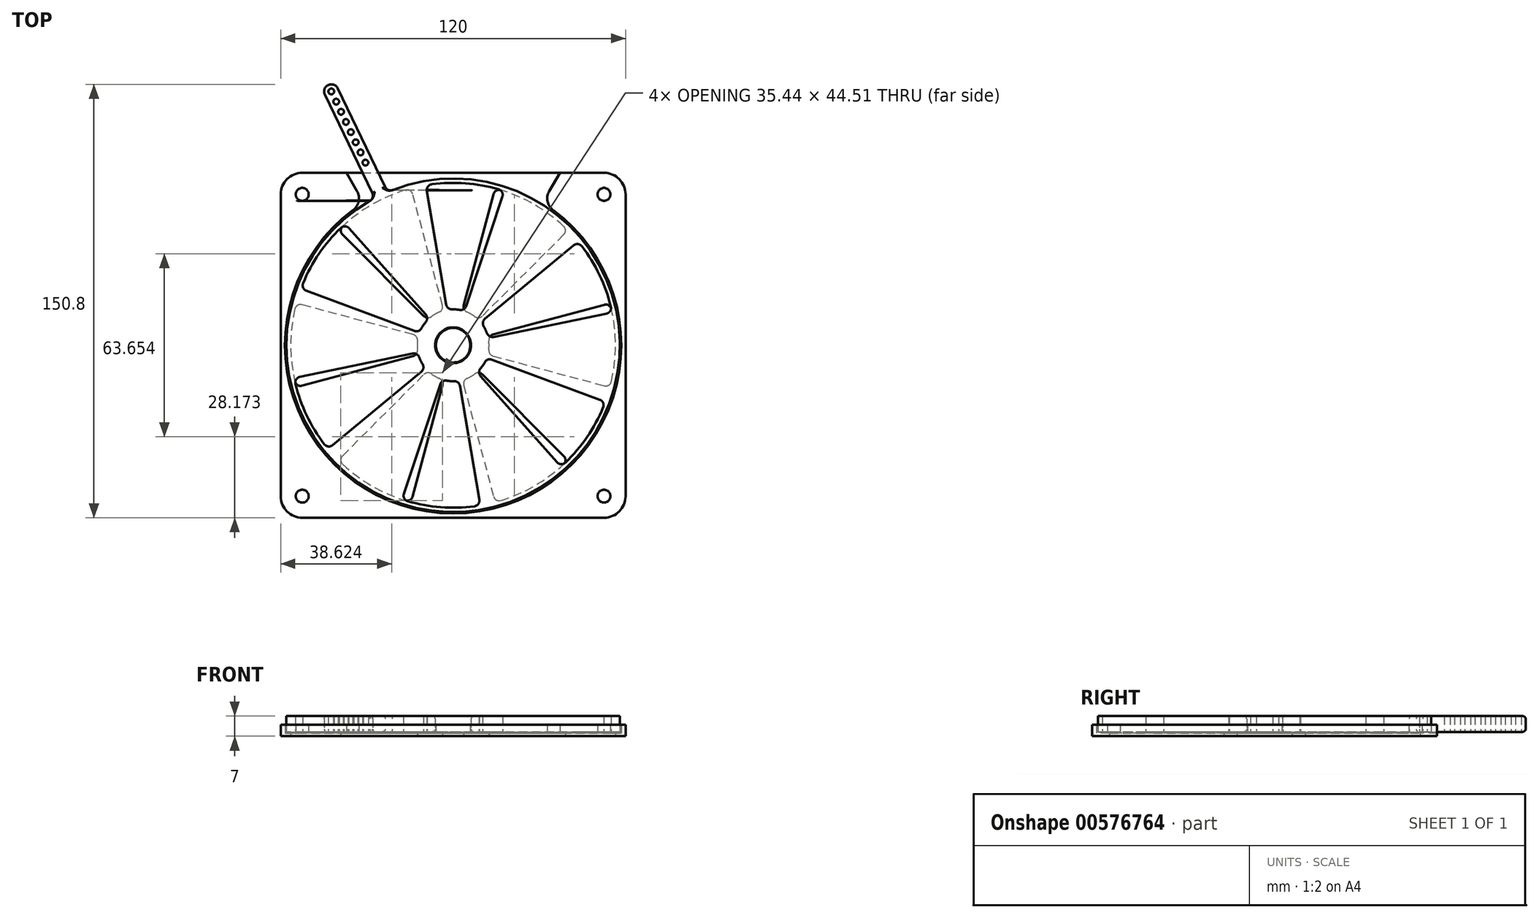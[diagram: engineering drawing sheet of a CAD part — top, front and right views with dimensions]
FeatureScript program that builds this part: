
annotation { "Feature Type Name" : "Feature", "Feature Type Description" : "" }
export const myFeature = defineFeature(function(context is Context, id is Id, definition is map)
    precondition{}
    {
        {
            var Q0;
            Q0=qCreatedBy(makeId("Top.planeOp"),FACE);
            var sketch = newSketch(context, id + "F0", { "sketchPlane" : qUnion([Q0])});
            skLineSegment(sketch, "E0.0", {"start": v(-52.5, 60) * mm, "end": v(52.5, 60) * mm});
            skLineSegment(sketch, "E0.1", {"start": v(-60, -52.5) * mm, "end": v(-60, 52.5) * mm});
            skLineSegment(sketch, "E0.2", {"start": v(-52.5, -60) * mm, "end": v(52.5, -60) * mm});
            skLineSegment(sketch, "E0.3", {"start": v(60, -52.5) * mm, "end": v(60, 52.5) * mm});
            skArc(sketch, "E1", {"start": v(52.5, 60) * mm, "mid": v(57.8, 57.8) * mm, "end": v(60, 52.5) * mm});
            skArc(sketch, "E2.1.1", {"start": v(-60, 52.5) * mm, "mid": v(-57.8, 57.8) * mm, "end": v(-52.5, 60) * mm});
            skArc(sketch, "E2.2.1", {"start": v(-52.5, -60) * mm, "mid": v(-57.8, -57.8) * mm, "end": v(-60, -52.5) * mm});
            skArc(sketch, "E2.3.1", {"start": v(60, -52.5) * mm, "mid": v(57.8, -57.8) * mm, "end": v(52.5, -60) * mm});
            skPoint(sketch, "E2.center", {"position": v(0, 0) * mm});
            skCircle(sketch, "E3", {"center": v(0, 0) * mm, "radius": 58.5 * mm});
            skCircle(sketch, "E4", {"center": v(-52.5, 52.5) * mm, "radius": 2.25 * mm});
            skCircle(sketch, "E5", {"center": v(52.5, 52.5) * mm, "radius": 2.25 * mm});
            skCircle(sketch, "E6", {"center": v(52.5, -52.5) * mm, "radius": 2.25 * mm});
            skCircle(sketch, "E7", {"center": v(-52.5, -52.5) * mm, "radius": 2.25 * mm});
            skCircle(sketch, "E8.0", {"center": v(0, 0) * mm, "radius": 56.5 * mm});
            skCircle(sketch, "E9", {"center": v(0, 0) * mm, "radius": 12.5 * mm});
            skLineSegment(sketch, "E10", {"start": v(-29.25, 50.66) * mm, "end": v(-34.64, 60) * mm});
            skLineSegment(sketch, "E11", {"start": v(29.25, 50.66) * mm, "end": v(34.64, 60) * mm});
            skLineSegment(sketch, "E12", {"start": v(-31.1, 49.55) * mm, "end": v(-37.14, 60) * mm});
            skLineSegment(sketch, "E13", {"start": v(37.14, 60) * mm, "end": v(31.1, 49.55) * mm});
            skCircle(sketch, "E14", {"center": v(0, 0) * mm, "radius": 6 * mm});
            skLineSegment(sketch, "E15.2.5.0", {"start": v(14.62, 54.57) * mm, "end": v(0, 0) * mm});
            skLineSegment(sketch, "E16.2.3.0", {"start": v(0, 0) * mm, "end": v(-14.62, 54.57) * mm});
            skLineSegment(sketch, "E17", {"start": v(-29.25, 50.66) * mm, "end": v(0, 0) * mm, "construction": true});
            skLineSegment(sketch, "E18.1.0", {"start": v(0, 0) * mm, "end": v(-54.57, 14.62) * mm});
            skLineSegment(sketch, "E18.1.1", {"start": v(-39.95, 39.95) * mm, "end": v(0, 0) * mm});
            skLineSegment(sketch, "E18.2.0", {"start": v(-39.95, -39.95) * mm, "end": v(0, 0) * mm});
            skLineSegment(sketch, "E18.2.1", {"start": v(-54.57, -14.62) * mm, "end": v(0, 0) * mm});
            skLineSegment(sketch, "E18.3.0", {"start": v(0, 0) * mm, "end": v(14.62, -54.57) * mm});
            skLineSegment(sketch, "E18.3.1", {"start": v(-14.62, -54.57) * mm, "end": v(0, 0) * mm});
            skLineSegment(sketch, "E18.4.0", {"start": v(0, 0) * mm, "end": v(54.57, -14.62) * mm});
            skLineSegment(sketch, "E18.4.1", {"start": v(39.95, -39.95) * mm, "end": v(0, 0) * mm});
            skLineSegment(sketch, "E18.5.0", {"start": v(39.95, 39.95) * mm, "end": v(0, 0) * mm});
            skLineSegment(sketch, "E18.5.1", {"start": v(54.57, 14.62) * mm, "end": v(0, 0) * mm});
            skLineSegment(sketch, "E19", {"start": v(29.25, 50.66) * mm, "end": v(0, 0) * mm, "construction": true});
            skSolve(sketch);
        }
        {
            var Q0;
            Q0=makeQuery(id+"F0.imprint","IMPRINT",FACE,{"disambiguationData":[TD([[makeQuery(id+"F0.imprint","IMPRINT",EDGE,{"derivedFrom":sQuery(id+"F0.wireOp",EDGE,"E0.1")}),-1.0]])]});
            extrude(context, id + "F1", {"entities" : qUnion([Q0]), "depth" : 4 * mm, "offsetDistance" : 25 * mm});
        }
        {
            var Q0;
            {var subQ0=sQuery(id+"F0.wireOp",EDGE,"E18.5.0");var subQ1=sQuery(id+"F0.wireOp",EDGE,"E9");var subQ2=makeQuery(id+"F0.imprint","INTERSECT",VERTEX,{"derivedFrom":[subQ1,subQ0]});Q0=makeQuery(id+"F0.imprint","IMPRINT",FACE,{"disambiguationData":[TD([[makeQuery(id+"F0.imprint","IMPRINT",EDGE,{"disambiguationData":[TD([[subQ2,1.0]])],"derivedFrom":subQ1}),1.0]])]});}
            var Q1;
            {var subQ0=sQuery(id+"F0.wireOp",EDGE,"E15.2.5.0");var subQ1=sQuery(id+"F0.wireOp",EDGE,"E9");var subQ2=makeQuery(id+"F0.imprint","INTERSECT",VERTEX,{"derivedFrom":[subQ1,subQ0]});Q1=makeQuery(id+"F0.imprint","IMPRINT",FACE,{"disambiguationData":[TD([[makeQuery(id+"F0.imprint","IMPRINT",EDGE,{"disambiguationData":[TD([[subQ2,-1.0]])],"derivedFrom":subQ1}),1.0]])]});}
            var Q2;
            {var subQ0=sQuery(id+"F0.wireOp",EDGE,"E16.2.3.0");var subQ1=sQuery(id+"F0.wireOp",EDGE,"E9");var subQ2=makeQuery(id+"F0.imprint","INTERSECT",VERTEX,{"derivedFrom":[subQ1,subQ0]});Q2=makeQuery(id+"F0.imprint","IMPRINT",FACE,{"disambiguationData":[TD([[makeQuery(id+"F0.imprint","IMPRINT",EDGE,{"disambiguationData":[TD([[subQ2,-1.0]])],"derivedFrom":subQ1}),1.0]])]});}
            var Q3;
            {var subQ0=sQuery(id+"F0.wireOp",EDGE,"E18.1.1");var subQ1=sQuery(id+"F0.wireOp",EDGE,"E9");var subQ2=makeQuery(id+"F0.imprint","INTERSECT",VERTEX,{"derivedFrom":[subQ1,subQ0]});Q3=makeQuery(id+"F0.imprint","IMPRINT",FACE,{"disambiguationData":[TD([[makeQuery(id+"F0.imprint","IMPRINT",EDGE,{"disambiguationData":[TD([[subQ2,-1.0]])],"derivedFrom":subQ1}),1.0]])]});}
            var Q4;
            {var subQ0=sQuery(id+"F0.wireOp",EDGE,"E18.1.0");var subQ1=sQuery(id+"F0.wireOp",EDGE,"E9");var subQ2=makeQuery(id+"F0.imprint","INTERSECT",VERTEX,{"derivedFrom":[subQ1,subQ0]});Q4=makeQuery(id+"F0.imprint","IMPRINT",FACE,{"disambiguationData":[TD([[makeQuery(id+"F0.imprint","IMPRINT",EDGE,{"disambiguationData":[TD([[subQ2,-1.0]])],"derivedFrom":subQ1}),1.0]])]});}
            var Q5;
            {var subQ0=sQuery(id+"F0.wireOp",EDGE,"E18.2.1");var subQ1=sQuery(id+"F0.wireOp",EDGE,"E9");var subQ2=makeQuery(id+"F0.imprint","INTERSECT",VERTEX,{"derivedFrom":[subQ1,subQ0]});Q5=makeQuery(id+"F0.imprint","IMPRINT",FACE,{"disambiguationData":[TD([[makeQuery(id+"F0.imprint","IMPRINT",EDGE,{"disambiguationData":[TD([[subQ2,-1.0]])],"derivedFrom":subQ1}),1.0]])]});}
            var Q6;
            {var subQ0=sQuery(id+"F0.wireOp",EDGE,"E18.2.0");var subQ1=sQuery(id+"F0.wireOp",EDGE,"E9");var subQ2=makeQuery(id+"F0.imprint","INTERSECT",VERTEX,{"derivedFrom":[subQ1,subQ0]});Q6=makeQuery(id+"F0.imprint","IMPRINT",FACE,{"disambiguationData":[TD([[makeQuery(id+"F0.imprint","IMPRINT",EDGE,{"disambiguationData":[TD([[subQ2,-1.0]])],"derivedFrom":subQ1}),1.0]])]});}
            var Q7;
            {var subQ0=sQuery(id+"F0.wireOp",EDGE,"E18.3.1");var subQ1=sQuery(id+"F0.wireOp",EDGE,"E9");var subQ2=makeQuery(id+"F0.imprint","INTERSECT",VERTEX,{"derivedFrom":[subQ1,subQ0]});Q7=makeQuery(id+"F0.imprint","IMPRINT",FACE,{"disambiguationData":[TD([[makeQuery(id+"F0.imprint","IMPRINT",EDGE,{"disambiguationData":[TD([[subQ2,-1.0]])],"derivedFrom":subQ1}),1.0]])]});}
            var Q8;
            {var subQ0=sQuery(id+"F0.wireOp",EDGE,"E18.3.0");var subQ1=sQuery(id+"F0.wireOp",EDGE,"E9");var subQ2=makeQuery(id+"F0.imprint","INTERSECT",VERTEX,{"derivedFrom":[subQ1,subQ0]});Q8=makeQuery(id+"F0.imprint","IMPRINT",FACE,{"disambiguationData":[TD([[makeQuery(id+"F0.imprint","IMPRINT",EDGE,{"disambiguationData":[TD([[subQ2,-1.0]])],"derivedFrom":subQ1}),1.0]])]});}
            var Q9;
            {var subQ0=sQuery(id+"F0.wireOp",EDGE,"E18.4.1");var subQ1=sQuery(id+"F0.wireOp",EDGE,"E9");var subQ2=makeQuery(id+"F0.imprint","INTERSECT",VERTEX,{"derivedFrom":[subQ1,subQ0]});Q9=makeQuery(id+"F0.imprint","IMPRINT",FACE,{"disambiguationData":[TD([[makeQuery(id+"F0.imprint","IMPRINT",EDGE,{"disambiguationData":[TD([[subQ2,-1.0]])],"derivedFrom":subQ1}),1.0]])]});}
            var Q10;
            {var subQ0=sQuery(id+"F0.wireOp",EDGE,"E18.5.1");var subQ1=sQuery(id+"F0.wireOp",EDGE,"E9");var subQ2=makeQuery(id+"F0.imprint","INTERSECT",VERTEX,{"derivedFrom":[subQ1,subQ0]});Q10=makeQuery(id+"F0.imprint","IMPRINT",FACE,{"disambiguationData":[TD([[makeQuery(id+"F0.imprint","IMPRINT",EDGE,{"disambiguationData":[TD([[subQ2,1.0]])],"derivedFrom":subQ1}),1.0]])]});}
            var Q11;
            {var subQ0=sQuery(id+"F0.wireOp",EDGE,"E11");Q11=makeQuery(id+"F0.imprint","IMPRINT",FACE,{"disambiguationData":[TD([[makeQuery(id+"F0.imprint","IMPRINT",EDGE,{"derivedFrom":subQ0}),-1.0]])]});}
            var Q12;
            {var subQ0=sQuery(id+"F0.wireOp",EDGE,"E18.5.0");var subQ1=sQuery(id+"F0.wireOp",EDGE,"E9");var subQ2=makeQuery(id+"F0.imprint","INTERSECT",VERTEX,{"derivedFrom":[subQ1,subQ0]});Q12=makeQuery(id+"F0.imprint","IMPRINT",FACE,{"disambiguationData":[TD([[makeQuery(id+"F0.imprint","IMPRINT",EDGE,{"disambiguationData":[TD([[subQ2,-1.0]])],"derivedFrom":subQ1}),1.0]])]});}
            var Q13;
            {var subQ0=sQuery(id+"F0.wireOp",EDGE,"E10");Q13=makeQuery(id+"F0.imprint","IMPRINT",FACE,{"disambiguationData":[TD([[makeQuery(id+"F0.imprint","IMPRINT",EDGE,{"derivedFrom":subQ0}),-1.0]])]});}
            var Q14;
            {var subQ6=sQuery(id+"F0.wireOp",EDGE,"E3");var subQ7=makeQuery(id+"F0.imprint","INTERSECT",VERTEX,{"derivedFrom":[subQ6,sQuery(id+"F0.wireOp",EDGE,"E11")]});Q14=makeQuery(id+"F0.imprint","IMPRINT",FACE,{"disambiguationData":[TD([[makeQuery(id+"F0.imprint","IMPRINT",EDGE,{"disambiguationData":[TD([[subQ7,1.0]])],"derivedFrom":subQ6}),1.0]])]});}
            var Q15;
            {var subQ0=sQuery(id+"F0.wireOp",EDGE,"E10");Q15=makeQuery(id+"F0.imprint","IMPRINT",FACE,{"disambiguationData":[TD([[makeQuery(id+"F0.imprint","IMPRINT",EDGE,{"derivedFrom":subQ0}),1.0]])]});}
            var Q16;
            {var subQ0=sQuery(id+"F0.wireOp",EDGE,"E18.5.0");var subQ1=sQuery(id+"F0.wireOp",EDGE,"E8.0");var subQ2=makeQuery(id+"F0.imprint","INTERSECT",VERTEX,{"derivedFrom":[subQ1,subQ0]});Q16=makeQuery(id+"F0.imprint","IMPRINT",FACE,{"disambiguationData":[TD([[makeQuery(id+"F0.imprint","IMPRINT",EDGE,{"disambiguationData":[TD([[subQ2,1.0]])],"derivedFrom":subQ1}),1.0]])]});}
            var Q17;
            {var subQ0=sQuery(id+"F0.wireOp",EDGE,"E18.4.0");var subQ1=sQuery(id+"F0.wireOp",EDGE,"E8.0");var subQ2=makeQuery(id+"F0.imprint","INTERSECT",VERTEX,{"derivedFrom":[subQ1,subQ0]});Q17=makeQuery(id+"F0.imprint","IMPRINT",FACE,{"disambiguationData":[TD([[makeQuery(id+"F0.imprint","IMPRINT",EDGE,{"disambiguationData":[TD([[subQ2,1.0]])],"derivedFrom":subQ1}),1.0]])]});}
            var Q18;
            {var subQ0=sQuery(id+"F0.wireOp",EDGE,"E18.3.0");var subQ1=sQuery(id+"F0.wireOp",EDGE,"E8.0");var subQ2=makeQuery(id+"F0.imprint","INTERSECT",VERTEX,{"derivedFrom":[subQ1,subQ0]});Q18=makeQuery(id+"F0.imprint","IMPRINT",FACE,{"disambiguationData":[TD([[makeQuery(id+"F0.imprint","IMPRINT",EDGE,{"disambiguationData":[TD([[subQ2,1.0]])],"derivedFrom":subQ1}),1.0]])]});}
            var Q19;
            {var subQ0=sQuery(id+"F0.wireOp",EDGE,"E18.2.0");var subQ1=sQuery(id+"F0.wireOp",EDGE,"E8.0");var subQ2=makeQuery(id+"F0.imprint","INTERSECT",VERTEX,{"derivedFrom":[subQ1,subQ0]});Q19=makeQuery(id+"F0.imprint","IMPRINT",FACE,{"disambiguationData":[TD([[makeQuery(id+"F0.imprint","IMPRINT",EDGE,{"disambiguationData":[TD([[subQ2,1.0]])],"derivedFrom":subQ1}),1.0]])]});}
            var Q20;
            {var subQ0=sQuery(id+"F0.wireOp",EDGE,"E18.1.0");var subQ1=sQuery(id+"F0.wireOp",EDGE,"E8.0");var subQ2=makeQuery(id+"F0.imprint","INTERSECT",VERTEX,{"derivedFrom":[subQ1,subQ0]});Q20=makeQuery(id+"F0.imprint","IMPRINT",FACE,{"disambiguationData":[TD([[makeQuery(id+"F0.imprint","IMPRINT",EDGE,{"disambiguationData":[TD([[subQ2,1.0]])],"derivedFrom":subQ1}),1.0]])]});}
            var Q21;
            {var subQ0=sQuery(id+"F0.wireOp",EDGE,"E15.2.5.0");var subQ1=sQuery(id+"F0.wireOp",EDGE,"E8.0");var subQ2=makeQuery(id+"F0.imprint","INTERSECT",VERTEX,{"derivedFrom":[subQ1,subQ0]});Q21=makeQuery(id+"F0.imprint","IMPRINT",FACE,{"disambiguationData":[TD([[makeQuery(id+"F0.imprint","IMPRINT",EDGE,{"disambiguationData":[TD([[subQ2,-1.0]])],"derivedFrom":subQ1}),1.0]])]});}
            extrude(context, id + "F2", {"entities" : qUnion([Q0, Q1, Q2, Q3, Q4, Q5, Q6, Q7, Q8, Q9, Q10, Q11, Q12, Q13, Q14, Q15, Q16, Q17, Q18, Q19, Q20, Q21]), "operationType" : NewBodyOperationType.ADD, "depth" : 1 * mm, "offsetDistance" : 25 * mm});
        }
        {
            var Q0;
            {var subQ0=sQuery(id+"F0.wireOp",EDGE,"E15.2.5.0");var subQ1=sQuery(id+"F0.wireOp",EDGE,"E14");var subQ2=makeQuery(id+"F0.imprint","INTERSECT",VERTEX,{"disambiguationData":[OD(1.0)],"derivedFrom":[subQ1,subQ0]});Q0=makeQuery(id+"F0.imprint","IMPRINT",FACE,{"disambiguationData":[TD([[makeQuery(id+"F0.imprint","IMPRINT",EDGE,{"disambiguationData":[TD([[subQ2,-1.0]])],"derivedFrom":subQ1}),1.0]])]});}
            var Q1;
            {var subQ0=sQuery(id+"F0.wireOp",EDGE,"E16.2.4.0");var subQ1=sQuery(id+"F0.wireOp",EDGE,"E14");var subQ2=makeQuery(id+"F0.imprint","INTERSECT",VERTEX,{"disambiguationData":[OD(1.0)],"derivedFrom":[subQ1,subQ0]});Q1=makeQuery(id+"F0.imprint","IMPRINT",FACE,{"disambiguationData":[TD([[makeQuery(id+"F0.imprint","IMPRINT",EDGE,{"disambiguationData":[TD([[subQ2,-1.0]])],"derivedFrom":subQ1}),1.0]])]});}
            var Q2;
            {var subQ0=sQuery(id+"F0.wireOp",EDGE,"E16.2.3.0");var subQ1=sQuery(id+"F0.wireOp",EDGE,"E14");var subQ2=makeQuery(id+"F0.imprint","INTERSECT",VERTEX,{"disambiguationData":[OD(1.0)],"derivedFrom":[subQ1,subQ0]});Q2=makeQuery(id+"F0.imprint","IMPRINT",FACE,{"disambiguationData":[TD([[makeQuery(id+"F0.imprint","IMPRINT",EDGE,{"disambiguationData":[TD([[subQ2,-1.0]])],"derivedFrom":subQ1}),1.0]])]});}
            var Q3;
            {var subQ0=sQuery(id+"F0.wireOp",EDGE,"874d3e22-e00a-4f2a-9944-a1ca78a42176.2.0");var subQ1=sQuery(id+"F0.wireOp",EDGE,"E14");var subQ2=makeQuery(id+"F0.imprint","INTERSECT",VERTEX,{"disambiguationData":[OD(1.0)],"derivedFrom":[subQ1,subQ0]});Q3=makeQuery(id+"F0.imprint","IMPRINT",FACE,{"disambiguationData":[TD([[makeQuery(id+"F0.imprint","IMPRINT",EDGE,{"disambiguationData":[TD([[subQ2,-1.0]])],"derivedFrom":subQ1}),1.0]])]});}
            var Q4;
            {var subQ0=sQuery(id+"F0.wireOp",EDGE,"E15.2.5.0");var subQ1=sQuery(id+"F0.wireOp",EDGE,"E14");var subQ2=makeQuery(id+"F0.imprint","INTERSECT",VERTEX,{"disambiguationData":[OD(0.0)],"derivedFrom":[subQ1,subQ0]});Q4=makeQuery(id+"F0.imprint","IMPRINT",FACE,{"disambiguationData":[TD([[makeQuery(id+"F0.imprint","IMPRINT",EDGE,{"disambiguationData":[TD([[subQ2,1.0]])],"derivedFrom":subQ1}),1.0]])]});}
            var Q5;
            {var subQ0=sQuery(id+"F0.wireOp",EDGE,"E16.2.5.0");var subQ1=sQuery(id+"F0.wireOp",EDGE,"E14");var subQ2=makeQuery(id+"F0.imprint","INTERSECT",VERTEX,{"disambiguationData":[OD(0.0)],"derivedFrom":[subQ1,subQ0]});Q5=makeQuery(id+"F0.imprint","IMPRINT",FACE,{"disambiguationData":[TD([[makeQuery(id+"F0.imprint","IMPRINT",EDGE,{"disambiguationData":[TD([[subQ2,1.0]])],"derivedFrom":subQ1}),1.0]])]});}
            var Q6;
            {var subQ0=sQuery(id+"F0.wireOp",EDGE,"E16.2.5.0");var subQ1=sQuery(id+"F0.wireOp",EDGE,"E14");var subQ2=makeQuery(id+"F0.imprint","INTERSECT",VERTEX,{"disambiguationData":[OD(0.0)],"derivedFrom":[subQ1,subQ0]});Q6=makeQuery(id+"F0.imprint","IMPRINT",FACE,{"disambiguationData":[TD([[makeQuery(id+"F0.imprint","IMPRINT",EDGE,{"disambiguationData":[TD([[subQ2,-1.0]])],"derivedFrom":subQ1}),1.0]])]});}
            var Q7;
            {var subQ0=sQuery(id+"F0.wireOp",EDGE,"E16.2.4.0");var subQ1=sQuery(id+"F0.wireOp",EDGE,"E14");var subQ2=makeQuery(id+"F0.imprint","INTERSECT",VERTEX,{"disambiguationData":[OD(0.0)],"derivedFrom":[subQ1,subQ0]});Q7=makeQuery(id+"F0.imprint","IMPRINT",FACE,{"disambiguationData":[TD([[makeQuery(id+"F0.imprint","IMPRINT",EDGE,{"disambiguationData":[TD([[subQ2,-1.0]])],"derivedFrom":subQ1}),1.0]])]});}
            var Q8;
            {var subQ0=sQuery(id+"F0.wireOp",EDGE,"E16.2.3.0");var subQ1=sQuery(id+"F0.wireOp",EDGE,"E14");var subQ2=makeQuery(id+"F0.imprint","INTERSECT",VERTEX,{"disambiguationData":[OD(0.0)],"derivedFrom":[subQ1,subQ0]});Q8=makeQuery(id+"F0.imprint","IMPRINT",FACE,{"disambiguationData":[TD([[makeQuery(id+"F0.imprint","IMPRINT",EDGE,{"disambiguationData":[TD([[subQ2,-1.0]])],"derivedFrom":subQ1}),1.0]])]});}
            var Q9;
            {var subQ0=sQuery(id+"F0.wireOp",EDGE,"874d3e22-e00a-4f2a-9944-a1ca78a42176.2.0");var subQ1=sQuery(id+"F0.wireOp",EDGE,"E14");var subQ2=makeQuery(id+"F0.imprint","INTERSECT",VERTEX,{"disambiguationData":[OD(0.0)],"derivedFrom":[subQ1,subQ0]});Q9=makeQuery(id+"F0.imprint","IMPRINT",FACE,{"disambiguationData":[TD([[makeQuery(id+"F0.imprint","IMPRINT",EDGE,{"disambiguationData":[TD([[subQ2,-1.0]])],"derivedFrom":subQ1}),1.0]])]});}
            var Q10;
            {var subQ0=sQuery(id+"F0.wireOp",EDGE,"874d3e22-e00a-4f2a-9944-a1ca78a42176.1.0");var subQ1=sQuery(id+"F0.wireOp",EDGE,"E14");var subQ2=makeQuery(id+"F0.imprint","INTERSECT",VERTEX,{"disambiguationData":[OD(0.0)],"derivedFrom":[subQ1,subQ0]});Q10=makeQuery(id+"F0.imprint","IMPRINT",FACE,{"disambiguationData":[TD([[makeQuery(id+"F0.imprint","IMPRINT",EDGE,{"disambiguationData":[TD([[subQ2,-1.0]])],"derivedFrom":subQ1}),1.0]])]});}
            var Q11;
            {var subQ0=sQuery(id+"F0.wireOp",EDGE,"E16.2.5.0");var subQ1=sQuery(id+"F0.wireOp",EDGE,"E14");var subQ2=makeQuery(id+"F0.imprint","INTERSECT",VERTEX,{"disambiguationData":[OD(1.0)],"derivedFrom":[subQ1,subQ0]});Q11=makeQuery(id+"F0.imprint","IMPRINT",FACE,{"disambiguationData":[TD([[makeQuery(id+"F0.imprint","IMPRINT",EDGE,{"disambiguationData":[TD([[subQ2,-1.0]])],"derivedFrom":subQ1}),1.0]])]});}
            extrude(context, id + "F3", {"entities" : qUnion([Q0, Q1, Q2, Q3, Q4, Q5, Q6, Q7, Q8, Q9, Q10, Q11]), "operationType" : NewBodyOperationType.ADD, "depth" : 4 * mm, "offsetDistance" : 25 * mm});
        }
        {
            var Q0;
            {var subQ0=sQuery(id+"F0.wireOp",EDGE,"E8.0");Q0=makeQuery(id+"F3.boolean.opBoolean","MERGE",FACE,{"derivedFrom":[makeQuery(id+"F2.opExtrude","CAP_FACE",FACE,{"disambiguationData":[OSD([sQuery(id+"F0.wireOp",EDGE,"E3"),subQ0])],"isStart":false}),makeQuery(id+"F3.opExtrude","CAP_FACE",FACE,{"disambiguationData":[OSD([subQ0,sQuery(id+"F0.wireOp",EDGE,"aZFLxbhU-lZEq-zJnE-4Ypo-IDTmSZkqapsP"),sQuery(id+"F0.wireOp",EDGE,"e7f66c59-8db4-4c02-a083-f046070294f7.1.0"),sQuery(id+"F0.wireOp",EDGE,"e7f66c59-8db4-4c02-a083-f046070294f7.2.0"),sQuery(id+"F0.wireOp",EDGE,"E9")])],"isStart":false})]});}
            var Q1;
            Q1=makeQuery(id+"F2.opExtrude","CAP_FACE",FACE,{"disambiguationData":[OSD([sQuery(id+"F0.wireOp",EDGE,"E0.0"),sQuery(id+"F0.wireOp",EDGE,"E3"),sQuery(id+"F0.wireOp",EDGE,"E8.0"),sQuery(id+"F0.wireOp",EDGE,"E9"),sQuery(id+"F0.wireOp",EDGE,"E12"),sQuery(id+"F0.wireOp",EDGE,"MmY6TyWV-4lzF-j9TC-Vc09-2jc4sYG30N3u"),sQuery(id+"F0.wireOp",EDGE,"E13"),sQuery(id+"F0.wireOp",EDGE,"E14"),sQuery(id+"F0.wireOp",EDGE,"E15.2.5.0"),sQuery(id+"F0.wireOp",EDGE,"874d3e22-e00a-4f2a-9944-a1ca78a42176.1.0"),sQuery(id+"F0.wireOp",EDGE,"874d3e22-e00a-4f2a-9944-a1ca78a42176.2.0"),sQuery(id+"F0.wireOp",EDGE,"E16.2.3.0"),sQuery(id+"F0.wireOp",EDGE,"E16.2.4.0"),sQuery(id+"F0.wireOp",EDGE,"E16.2.5.0")])],"isStart":false});
            cPlane(context, id + "F4", {"entities" : qUnion([Q0, Q1]), "cplaneType" : CPlaneType.OFFSET, "offset" : .5 * mm, "width" : 150 * mm, "height" : 150 * mm});
        }
        {
            var Q0;
            Q0=qCreatedBy(id+"F4.planeOp",FACE);
            var sketch = newSketch(context, id + "F5", { "sketchPlane" : qUnion([Q0])});
            skArc(sketch, "E20.1", {"start": v(3.94, 11.86) * mm, "mid": v(0.95, 12.46) * mm, "end": v(-2.1, 12.32) * mm});
            skLineSegment(sketch, "E20.2", {"start": v(-2.1, 12.32) * mm, "end": v(-9.47, 55.7) * mm});
            skArc(sketch, "E20.3", {"start": v(17.8, 53.63) * mm, "mid": v(4.29, 56.34) * mm, "end": v(-9.47, 55.7) * mm});
            skCircle(sketch, "E21", {"center": v(0, 0) * mm, "radius": 58 * mm});
            skLineSegment(sketch, "E22", {"start": v(3.94, 11.86) * mm, "end": v(17.8, 53.63) * mm});
            skLineSegment(sketch, "E23", {"start": v(-27.33, 51.16) * mm, "end": v(-44.65, 87.21) * mm});
            skLineSegment(sketch, "E24", {"start": v(-22.83, 53.32) * mm, "end": v(-40.14, 89.38) * mm});
            skArc(sketch, "E25", {"start": v(-44.65, 87.21) * mm, "mid": v(-43.47, 90.55) * mm, "end": v(-40.14, 89.38) * mm});
            skCircle(sketch, "E26", {"center": v(-42.4, 88.3) * mm, "radius": 1 * mm});
            skLineSegment(sketch, "E27", {"start": v(-42.4, 88.3) * mm, "end": v(-25.1, 52.29) * mm, "construction": true});
            skCircle(sketch, "E28", {"center": v(0, 0) * mm, "radius": 6.25 * mm});
            skCircle(sketch, "E29.1.0.0", {"center": v(-40.7, 84.76) * mm, "radius": 1 * mm});
            skCircle(sketch, "E29.2.0.0", {"center": v(-39, 81.23) * mm, "radius": 1 * mm});
            skCircle(sketch, "E29.3.0.0", {"center": v(-37.3, 77.7) * mm, "radius": 1 * mm});
            skCircle(sketch, "E29.4.0.0", {"center": v(-35.6, 74.16) * mm, "radius": 1 * mm});
            skCircle(sketch, "E29.5.0.0", {"center": v(-33.9, 70.62) * mm, "radius": 1 * mm});
            skLineSegment(sketch, "E29.direction1", {"start": v(-42.4, 88.3) * mm, "end": v(-40.7, 84.78) * mm, "construction": true});
            skCircle(sketch, "E30.0.6.0", {"center": v(-32.21, 67.09) * mm, "radius": 1 * mm});
            skCircle(sketch, "E30.0.7.0", {"center": v(-30.51, 63.55) * mm, "radius": 1 * mm});
            skLineSegment(sketch, "E31", {"start": v(-2.1, 12.32) * mm, "end": v(0, 0) * mm, "construction": true});
            skLineSegment(sketch, "E32", {"start": v(3.94, 11.86) * mm, "end": v(0, 0) * mm, "construction": true});
            skLineSegment(sketch, "E33", {"start": v(-25.1, 52.29) * mm, "end": v(-30.51, 63.55) * mm});
            skLineSegment(sketch, "E34.1.0", {"start": v(-8.3, 9.34) * mm, "end": v(-37.55, 42.22) * mm});
            skArc(sketch, "E34.1.1", {"start": v(-37.55, 42.22) * mm, "mid": v(-46.64, 31.88) * mm, "end": v(-52.97, 19.65) * mm});
            skLineSegment(sketch, "E34.1.2", {"start": v(-11.72, 4.35) * mm, "end": v(-52.97, 19.65) * mm});
            skLineSegment(sketch, "E34.1.3", {"start": v(-11.72, 4.35) * mm, "end": v(0, 0) * mm, "construction": true});
            skArc(sketch, "E34.1.4", {"start": v(-8.3, 9.34) * mm, "mid": v(-10.32, 7.05) * mm, "end": v(-11.72, 4.35) * mm});
            skLineSegment(sketch, "E34.1.5", {"start": v(-8.3, 9.34) * mm, "end": v(0, 0) * mm, "construction": true});
            skLineSegment(sketch, "E34.2.0", {"start": v(-12.24, -2.52) * mm, "end": v(-55.34, -11.4) * mm});
            skArc(sketch, "E34.2.1", {"start": v(-55.34, -11.4) * mm, "mid": v(-50.93, -24.45) * mm, "end": v(-43.5, -36.05) * mm});
            skLineSegment(sketch, "E34.2.2", {"start": v(-9.63, -7.98) * mm, "end": v(-43.5, -36.05) * mm});
            skLineSegment(sketch, "E34.2.3", {"start": v(-9.63, -7.98) * mm, "end": v(0, 0) * mm, "construction": true});
            skArc(sketch, "E34.2.4", {"start": v(-12.24, -2.52) * mm, "mid": v(-11.27, -5.41) * mm, "end": v(-9.63, -7.98) * mm});
            skLineSegment(sketch, "E34.2.5", {"start": v(-12.24, -2.52) * mm, "end": v(0, 0) * mm, "construction": true});
            skLineSegment(sketch, "E34.3.0", {"start": v(-3.94, -11.86) * mm, "end": v(-17.8, -53.63) * mm});
            skArc(sketch, "E34.3.1", {"start": v(-17.8, -53.63) * mm, "mid": v(-4.29, -56.34) * mm, "end": v(9.47, -55.7) * mm});
            skLineSegment(sketch, "E34.3.2", {"start": v(2.1, -12.32) * mm, "end": v(9.47, -55.7) * mm});
            skLineSegment(sketch, "E34.3.3", {"start": v(2.1, -12.32) * mm, "end": v(0, 0) * mm, "construction": true});
            skArc(sketch, "E34.3.4", {"start": v(-3.94, -11.86) * mm, "mid": v(-0.95, -12.46) * mm, "end": v(2.1, -12.32) * mm});
            skLineSegment(sketch, "E34.3.5", {"start": v(-3.94, -11.86) * mm, "end": v(0, 0) * mm, "construction": true});
            skLineSegment(sketch, "E34.4.0", {"start": v(8.3, -9.34) * mm, "end": v(37.55, -42.22) * mm});
            skArc(sketch, "E34.4.1", {"start": v(37.55, -42.22) * mm, "mid": v(46.64, -31.88) * mm, "end": v(52.97, -19.65) * mm});
            skLineSegment(sketch, "E34.4.2", {"start": v(11.72, -4.35) * mm, "end": v(52.97, -19.65) * mm});
            skLineSegment(sketch, "E34.4.3", {"start": v(11.72, -4.35) * mm, "end": v(0, 0) * mm, "construction": true});
            skArc(sketch, "E34.4.4", {"start": v(8.3, -9.34) * mm, "mid": v(10.32, -7.05) * mm, "end": v(11.72, -4.35) * mm});
            skLineSegment(sketch, "E34.4.5", {"start": v(8.3, -9.34) * mm, "end": v(0, 0) * mm, "construction": true});
            skLineSegment(sketch, "E34.5.0", {"start": v(12.24, 2.52) * mm, "end": v(55.34, 11.4) * mm});
            skArc(sketch, "E34.5.1", {"start": v(55.34, 11.4) * mm, "mid": v(50.93, 24.45) * mm, "end": v(43.5, 36.05) * mm});
            skLineSegment(sketch, "E34.5.2", {"start": v(9.63, 7.98) * mm, "end": v(43.5, 36.05) * mm});
            skLineSegment(sketch, "E34.5.3", {"start": v(9.63, 7.98) * mm, "end": v(0, 0) * mm, "construction": true});
            skArc(sketch, "E34.5.4", {"start": v(12.24, 2.52) * mm, "mid": v(11.27, 5.41) * mm, "end": v(9.63, 7.98) * mm});
            skLineSegment(sketch, "E34.5.5", {"start": v(12.24, 2.52) * mm, "end": v(0, 0) * mm, "construction": true});
            skSolve(sketch);
        }
        {
            var Q0;
            Q0=makeQuery(id+"F5.imprint","IMPRINT",FACE,{"disambiguationData":[TD([[makeQuery(id+"F5.imprint","IMPRINT",EDGE,{"derivedFrom":sQuery(id+"F5.wireOp",EDGE,"E20.1")}),1.0]])]});
            var Q1;
            {var subQ0=sQuery(id+"F5.wireOp",EDGE,"E23");Q1=makeQuery(id+"F5.imprint","IMPRINT",FACE,{"disambiguationData":[TD([[makeQuery(id+"F5.imprint","IMPRINT",EDGE,{"derivedFrom":subQ0}),-1.0]])]});}
            extrude(context, id + "F6", {"entities" : qUnion([Q0, Q1]), "depth" : 5.5 * mm, "offsetDistance" : 25 * mm});
        }
        {
            var Q0;
            Q0=makeQuery(id+"F6.opExtrude","CAP_EDGE",EDGE,{"disambiguationData":[OSD([sQuery(id+"F5.wireOp",EDGE,"E25")])],"isStart":false});
            var Q1;
            Q1=makeQuery(id+"F6.opExtrude","CAP_EDGE",EDGE,{"disambiguationData":[OSD([sQuery(id+"F5.wireOp",EDGE,"E24")])],"isStart":false});
            var Q2;
            Q2=makeQuery(id+"F6.opExtrude","CAP_EDGE",EDGE,{"disambiguationData":[OSD([sQuery(id+"F5.wireOp",EDGE,"E23")])],"isStart":false});
            var Q3;
            Q3=makeQuery(id+"F6.opExtrude","CAP_EDGE",EDGE,{"disambiguationData":[OSD([sQuery(id+"F5.wireOp",EDGE,"E24")])],"isStart":true});
            var Q4;
            Q4=makeQuery(id+"F6.opExtrude","CAP_EDGE",EDGE,{"disambiguationData":[OSD([sQuery(id+"F5.wireOp",EDGE,"E25")])],"isStart":true});
            var Q5;
            Q5=makeQuery(id+"F6.opExtrude","CAP_EDGE",EDGE,{"disambiguationData":[OSD([sQuery(id+"F5.wireOp",EDGE,"E23")])],"isStart":true});
            fillet(context, id + "F7", {"entities" : qUnion([Q0, Q1, Q2, Q3, Q4, Q5]), "radius" : 1 * mm, "tangentPropagation" : true, "allowEdgeOverflow" : false});
        }
        {
            var Q0;
            Q0=makeQuery(id+"F6.opExtrude","SWEPT_EDGE",EDGE,{"disambiguationData":[OSD([sQuery(id+"F5.wireOp",EDGE,"E34.2.0"),sQuery(id+"F5.wireOp",EDGE,"E34.2.1")])]});
            var Q1;
            Q1=makeQuery(id+"F6.opExtrude","SWEPT_EDGE",EDGE,{"disambiguationData":[OSD([sQuery(id+"F5.wireOp",EDGE,"E34.1.1"),sQuery(id+"F5.wireOp",EDGE,"E34.1.2")])]});
            var Q2;
            Q2=makeQuery(id+"F6.opExtrude","SWEPT_EDGE",EDGE,{"disambiguationData":[OSD([sQuery(id+"F5.wireOp",EDGE,"E34.3.0"),sQuery(id+"F5.wireOp",EDGE,"E34.3.1")])]});
            var Q3;
            Q3=makeQuery(id+"F6.opExtrude","SWEPT_EDGE",EDGE,{"disambiguationData":[OSD([sQuery(id+"F5.wireOp",EDGE,"E34.4.0"),sQuery(id+"F5.wireOp",EDGE,"E34.4.4")])]});
            var Q4;
            Q4=makeQuery(id+"F6.opExtrude","SWEPT_EDGE",EDGE,{"disambiguationData":[OSD([sQuery(id+"F5.wireOp",EDGE,"E34.5.2"),sQuery(id+"F5.wireOp",EDGE,"E34.5.4")])]});
            var Q5;
            Q5=makeQuery(id+"F6.opExtrude","SWEPT_EDGE",EDGE,{"disambiguationData":[OSD([sQuery(id+"F5.wireOp",EDGE,"E34.2.1"),sQuery(id+"F5.wireOp",EDGE,"E34.2.2")])]});
            var Q6;
            Q6=makeQuery(id+"F6.opExtrude","SWEPT_EDGE",EDGE,{"disambiguationData":[OSD([sQuery(id+"F5.wireOp",EDGE,"E20.1"),sQuery(id+"F5.wireOp",EDGE,"E22")])]});
            var Q7;
            Q7=makeQuery(id+"F6.opExtrude","SWEPT_EDGE",EDGE,{"disambiguationData":[OSD([sQuery(id+"F5.wireOp",EDGE,"E20.1"),sQuery(id+"F5.wireOp",EDGE,"E20.2")])]});
            var Q8;
            Q8=makeQuery(id+"F6.opExtrude","SWEPT_EDGE",EDGE,{"disambiguationData":[OSD([sQuery(id+"F5.wireOp",EDGE,"E34.1.2"),sQuery(id+"F5.wireOp",EDGE,"E34.1.4")])]});
            var Q9;
            Q9=makeQuery(id+"F6.opExtrude","SWEPT_EDGE",EDGE,{"disambiguationData":[OSD([sQuery(id+"F5.wireOp",EDGE,"E21"),sQuery(id+"F5.wireOp",EDGE,"E24")])]});
            var Q10;
            Q10=makeQuery(id+"F6.opExtrude","SWEPT_EDGE",EDGE,{"disambiguationData":[OSD([sQuery(id+"F5.wireOp",EDGE,"E21"),sQuery(id+"F5.wireOp",EDGE,"E23")])]});
            var Q11;
            Q11=makeQuery(id+"F6.opExtrude","SWEPT_EDGE",EDGE,{"disambiguationData":[OSD([sQuery(id+"F5.wireOp",EDGE,"E34.1.0"),sQuery(id+"F5.wireOp",EDGE,"E34.1.4")])]});
            var Q12;
            Q12=makeQuery(id+"F6.opExtrude","SWEPT_EDGE",EDGE,{"disambiguationData":[OSD([sQuery(id+"F5.wireOp",EDGE,"E34.2.2"),sQuery(id+"F5.wireOp",EDGE,"E34.2.4")])]});
            var Q13;
            Q13=makeQuery(id+"F6.opExtrude","SWEPT_EDGE",EDGE,{"disambiguationData":[OSD([sQuery(id+"F5.wireOp",EDGE,"E34.5.0"),sQuery(id+"F5.wireOp",EDGE,"E34.5.1")])]});
            var Q14;
            Q14=makeQuery(id+"F6.opExtrude","SWEPT_EDGE",EDGE,{"disambiguationData":[OSD([sQuery(id+"F5.wireOp",EDGE,"E34.3.1"),sQuery(id+"F5.wireOp",EDGE,"E34.3.2")])]});
            var Q15;
            Q15=makeQuery(id+"F6.opExtrude","SWEPT_EDGE",EDGE,{"disambiguationData":[OSD([sQuery(id+"F5.wireOp",EDGE,"E20.3"),sQuery(id+"F5.wireOp",EDGE,"E22")])]});
            var Q16;
            Q16=makeQuery(id+"F6.opExtrude","SWEPT_EDGE",EDGE,{"disambiguationData":[OSD([sQuery(id+"F5.wireOp",EDGE,"E34.4.1"),sQuery(id+"F5.wireOp",EDGE,"E34.4.2")])]});
            var Q17;
            Q17=makeQuery(id+"F6.opExtrude","SWEPT_EDGE",EDGE,{"disambiguationData":[OSD([sQuery(id+"F5.wireOp",EDGE,"E34.5.1"),sQuery(id+"F5.wireOp",EDGE,"E34.5.2")])]});
            var Q18;
            Q18=makeQuery(id+"F6.opExtrude","SWEPT_EDGE",EDGE,{"disambiguationData":[OSD([sQuery(id+"F5.wireOp",EDGE,"E34.2.0"),sQuery(id+"F5.wireOp",EDGE,"E34.2.4")])]});
            var Q19;
            Q19=makeQuery(id+"F6.opExtrude","SWEPT_EDGE",EDGE,{"disambiguationData":[OSD([sQuery(id+"F5.wireOp",EDGE,"E34.3.2"),sQuery(id+"F5.wireOp",EDGE,"E34.3.4")])]});
            var Q20;
            Q20=makeQuery(id+"F6.opExtrude","SWEPT_EDGE",EDGE,{"disambiguationData":[OSD([sQuery(id+"F5.wireOp",EDGE,"E34.4.2"),sQuery(id+"F5.wireOp",EDGE,"E34.4.4")])]});
            var Q21;
            Q21=makeQuery(id+"F6.opExtrude","SWEPT_EDGE",EDGE,{"disambiguationData":[OSD([sQuery(id+"F5.wireOp",EDGE,"E34.3.0"),sQuery(id+"F5.wireOp",EDGE,"E34.3.4")])]});
            var Q22;
            Q22=makeQuery(id+"F6.opExtrude","SWEPT_EDGE",EDGE,{"disambiguationData":[OSD([sQuery(id+"F5.wireOp",EDGE,"E34.1.0"),sQuery(id+"F5.wireOp",EDGE,"E34.1.1")])]});
            var Q23;
            Q23=makeQuery(id+"F6.opExtrude","SWEPT_EDGE",EDGE,{"disambiguationData":[OSD([sQuery(id+"F5.wireOp",EDGE,"E20.2"),sQuery(id+"F5.wireOp",EDGE,"E20.3")])]});
            var Q24;
            Q24=makeQuery(id+"F6.opExtrude","SWEPT_EDGE",EDGE,{"disambiguationData":[OSD([sQuery(id+"F5.wireOp",EDGE,"E34.4.0"),sQuery(id+"F5.wireOp",EDGE,"E34.4.1")])]});
            var Q25;
            Q25=makeQuery(id+"F6.opExtrude","SWEPT_EDGE",EDGE,{"disambiguationData":[OSD([sQuery(id+"F5.wireOp",EDGE,"E34.5.0"),sQuery(id+"F5.wireOp",EDGE,"E34.5.4")])]});
            fillet(context, id + "F8", {"entities" : qUnion([Q0, Q1, Q2, Q3, Q4, Q5, Q6, Q7, Q8, Q9, Q10, Q11, Q12, Q13, Q14, Q15, Q16, Q17, Q18, Q19, Q20, Q21, Q22, Q23, Q24, Q25]), "radius" : 2 * mm, "tangentPropagation" : true, "allowEdgeOverflow" : false});
        }
        {
            var Q0;
            {var subQ0=sQuery(id+"F0.wireOp",EDGE,"E15.2.5.0");var subQ1=sQuery(id+"F0.wireOp",EDGE,"E9");Q0=makeQuery(id+"F2.opExtrude","SWEPT_EDGE",EDGE,{"disambiguationData":[OSD([subQ1,subQ0]),TDD([makeQuery(id+"F0.imprint","INTERSECT",VERTEX,{"disambiguationData":[OD(0.0)],"derivedFrom":[subQ1,subQ0]})])]});}
            var Q1;
            {var subQ0=sQuery(id+"F0.wireOp",EDGE,"E16.2.5.0");var subQ1=sQuery(id+"F0.wireOp",EDGE,"E9");Q1=makeQuery(id+"F2.opExtrude","SWEPT_EDGE",EDGE,{"disambiguationData":[OSD([subQ1,subQ0]),TDD([makeQuery(id+"F0.imprint","INTERSECT",VERTEX,{"disambiguationData":[OD(0.0)],"derivedFrom":[subQ1,subQ0]})])]});}
            var Q2;
            {var subQ0=sQuery(id+"F0.wireOp",EDGE,"874d3e22-e00a-4f2a-9944-a1ca78a42176.1.0");var subQ1=sQuery(id+"F0.wireOp",EDGE,"E9");Q2=makeQuery(id+"F2.opExtrude","SWEPT_EDGE",EDGE,{"disambiguationData":[OSD([subQ1,subQ0]),TDD([makeQuery(id+"F0.imprint","INTERSECT",VERTEX,{"disambiguationData":[OD(1.0)],"derivedFrom":[subQ1,subQ0]})])]});}
            var Q3;
            {var subQ0=sQuery(id+"F0.wireOp",EDGE,"874d3e22-e00a-4f2a-9944-a1ca78a42176.2.0");var subQ1=sQuery(id+"F0.wireOp",EDGE,"E9");Q3=makeQuery(id+"F2.opExtrude","SWEPT_EDGE",EDGE,{"disambiguationData":[OSD([subQ1,subQ0]),TDD([makeQuery(id+"F0.imprint","INTERSECT",VERTEX,{"disambiguationData":[OD(1.0)],"derivedFrom":[subQ1,subQ0]})])]});}
            var Q4;
            {var subQ0=sQuery(id+"F0.wireOp",EDGE,"E16.2.4.0");var subQ1=sQuery(id+"F0.wireOp",EDGE,"E9");Q4=makeQuery(id+"F2.opExtrude","SWEPT_EDGE",EDGE,{"disambiguationData":[OSD([subQ1,subQ0]),TDD([makeQuery(id+"F0.imprint","INTERSECT",VERTEX,{"disambiguationData":[OD(1.0)],"derivedFrom":[subQ1,subQ0]})])]});}
            var Q5;
            {var subQ0=sQuery(id+"F0.wireOp",EDGE,"E16.2.3.0");var subQ1=sQuery(id+"F0.wireOp",EDGE,"E9");Q5=makeQuery(id+"F2.opExtrude","SWEPT_EDGE",EDGE,{"disambiguationData":[OSD([subQ1,subQ0]),TDD([makeQuery(id+"F0.imprint","INTERSECT",VERTEX,{"disambiguationData":[OD(1.0)],"derivedFrom":[subQ1,subQ0]})])]});}
            var Q6;
            {var subQ0=sQuery(id+"F0.wireOp",EDGE,"E15.2.5.0");var subQ1=sQuery(id+"F0.wireOp",EDGE,"E9");Q6=makeQuery(id+"F2.opExtrude","SWEPT_EDGE",EDGE,{"disambiguationData":[OSD([subQ1,subQ0]),TDD([makeQuery(id+"F0.imprint","INTERSECT",VERTEX,{"disambiguationData":[OD(1.0)],"derivedFrom":[subQ1,subQ0]})])]});}
            var Q7;
            {var subQ0=sQuery(id+"F0.wireOp",EDGE,"E16.2.5.0");var subQ1=sQuery(id+"F0.wireOp",EDGE,"E9");Q7=makeQuery(id+"F2.opExtrude","SWEPT_EDGE",EDGE,{"disambiguationData":[OSD([subQ1,subQ0]),TDD([makeQuery(id+"F0.imprint","INTERSECT",VERTEX,{"disambiguationData":[OD(1.0)],"derivedFrom":[subQ1,subQ0]})])]});}
            var Q8;
            {var subQ0=sQuery(id+"F0.wireOp",EDGE,"874d3e22-e00a-4f2a-9944-a1ca78a42176.2.0");var subQ1=sQuery(id+"F0.wireOp",EDGE,"E9");Q8=makeQuery(id+"F2.opExtrude","SWEPT_EDGE",EDGE,{"disambiguationData":[OSD([subQ1,subQ0]),TDD([makeQuery(id+"F0.imprint","INTERSECT",VERTEX,{"disambiguationData":[OD(0.0)],"derivedFrom":[subQ1,subQ0]})])]});}
            var Q9;
            {var subQ0=sQuery(id+"F0.wireOp",EDGE,"874d3e22-e00a-4f2a-9944-a1ca78a42176.1.0");var subQ1=sQuery(id+"F0.wireOp",EDGE,"E9");Q9=makeQuery(id+"F2.opExtrude","SWEPT_EDGE",EDGE,{"disambiguationData":[OSD([subQ1,subQ0]),TDD([makeQuery(id+"F0.imprint","INTERSECT",VERTEX,{"disambiguationData":[OD(0.0)],"derivedFrom":[subQ1,subQ0]})])]});}
            var Q10;
            {var subQ0=sQuery(id+"F0.wireOp",EDGE,"E16.2.4.0");var subQ1=sQuery(id+"F0.wireOp",EDGE,"E9");Q10=makeQuery(id+"F2.opExtrude","SWEPT_EDGE",EDGE,{"disambiguationData":[OSD([subQ1,subQ0]),TDD([makeQuery(id+"F0.imprint","INTERSECT",VERTEX,{"disambiguationData":[OD(0.0)],"derivedFrom":[subQ1,subQ0]})])]});}
            var Q11;
            {var subQ0=sQuery(id+"F0.wireOp",EDGE,"E16.2.3.0");var subQ1=sQuery(id+"F0.wireOp",EDGE,"E9");Q11=makeQuery(id+"F2.opExtrude","SWEPT_EDGE",EDGE,{"disambiguationData":[OSD([subQ1,subQ0]),TDD([makeQuery(id+"F0.imprint","INTERSECT",VERTEX,{"disambiguationData":[OD(0.0)],"derivedFrom":[subQ1,subQ0]})])]});}
            var Q12;
            Q12=makeQuery(id+"F2.opExtrude","SWEPT_EDGE",EDGE,{"disambiguationData":[OSD([sQuery(id+"F0.wireOp",EDGE,"E8.0"),sQuery(id+"F0.wireOp",EDGE,"E16.2.4.0")])]});
            var Q13;
            {var subQ0=sQuery(id+"F0.wireOp",EDGE,"E16.2.5.0");var subQ1=sQuery(id+"F0.wireOp",EDGE,"E8.0");Q13=makeQuery(id+"F2.opExtrude","SWEPT_EDGE",EDGE,{"disambiguationData":[OSD([subQ1,subQ0]),TDD([makeQuery(id+"F0.imprint","INTERSECT",VERTEX,{"disambiguationData":[OD(0.0)],"derivedFrom":[subQ1,subQ0]})])]});}
            var Q14;
            Q14=makeQuery(id+"F2.opExtrude","SWEPT_EDGE",EDGE,{"disambiguationData":[OSD([sQuery(id+"F0.wireOp",EDGE,"E8.0"),sQuery(id+"F0.wireOp",EDGE,"874d3e22-e00a-4f2a-9944-a1ca78a42176.2.0")])]});
            var Q15;
            {var subQ0=sQuery(id+"F0.wireOp",EDGE,"E15.2.5.0");var subQ1=sQuery(id+"F0.wireOp",EDGE,"E8.0");Q15=makeQuery(id+"F2.opExtrude","SWEPT_EDGE",EDGE,{"disambiguationData":[OSD([subQ1,subQ0]),TDD([makeQuery(id+"F0.imprint","INTERSECT",VERTEX,{"disambiguationData":[OD(0.0)],"derivedFrom":[subQ1,subQ0]})])]});}
            var Q16;
            {var subQ0=sQuery(id+"F0.wireOp",EDGE,"E16.2.3.0");var subQ1=sQuery(id+"F0.wireOp",EDGE,"E8.0");Q16=makeQuery(id+"F2.opExtrude","SWEPT_EDGE",EDGE,{"disambiguationData":[OSD([subQ1,subQ0]),TDD([makeQuery(id+"F0.imprint","INTERSECT",VERTEX,{"disambiguationData":[OD(0.0)],"derivedFrom":[subQ1,subQ0]})])]});}
            var Q17;
            {var subQ0=sQuery(id+"F0.wireOp",EDGE,"874d3e22-e00a-4f2a-9944-a1ca78a42176.1.0");var subQ1=sQuery(id+"F0.wireOp",EDGE,"E8.0");Q17=makeQuery(id+"F2.opExtrude","SWEPT_EDGE",EDGE,{"disambiguationData":[OSD([subQ1,subQ0]),TDD([makeQuery(id+"F0.imprint","INTERSECT",VERTEX,{"disambiguationData":[OD(0.0)],"derivedFrom":[subQ1,subQ0]})])]});}
            var Q18;
            {var subQ0=sQuery(id+"F0.wireOp",EDGE,"E16.2.5.0");var subQ1=sQuery(id+"F0.wireOp",EDGE,"E8.0");Q18=makeQuery(id+"F2.opExtrude","SWEPT_EDGE",EDGE,{"disambiguationData":[OSD([subQ1,subQ0]),TDD([makeQuery(id+"F0.imprint","INTERSECT",VERTEX,{"disambiguationData":[OD(1.0)],"derivedFrom":[subQ1,subQ0]})])]});}
            var Q19;
            Q19=makeQuery(id+"F2.opExtrude","SWEPT_EDGE",EDGE,{"disambiguationData":[OSD([sQuery(id+"F0.wireOp",EDGE,"E8.0"),sQuery(id+"F0.wireOp",EDGE,"E11"),sQuery(id+"F0.wireOp",EDGE,"E16.2.4.0")])]});
            var Q20;
            Q20=makeQuery(id+"F2.opExtrude","SWEPT_EDGE",EDGE,{"disambiguationData":[OSD([sQuery(id+"F0.wireOp",EDGE,"E8.0"),sQuery(id+"F0.wireOp",EDGE,"E10"),sQuery(id+"F0.wireOp",EDGE,"874d3e22-e00a-4f2a-9944-a1ca78a42176.2.0")])]});
            var Q21;
            {var subQ0=sQuery(id+"F0.wireOp",EDGE,"874d3e22-e00a-4f2a-9944-a1ca78a42176.1.0");var subQ1=sQuery(id+"F0.wireOp",EDGE,"E8.0");Q21=makeQuery(id+"F2.opExtrude","SWEPT_EDGE",EDGE,{"disambiguationData":[OSD([subQ1,subQ0]),TDD([makeQuery(id+"F0.imprint","INTERSECT",VERTEX,{"disambiguationData":[OD(1.0)],"derivedFrom":[subQ1,subQ0]})])]});}
            var Q22;
            {var subQ0=sQuery(id+"F0.wireOp",EDGE,"E16.2.3.0");var subQ1=sQuery(id+"F0.wireOp",EDGE,"E8.0");Q22=makeQuery(id+"F2.opExtrude","SWEPT_EDGE",EDGE,{"disambiguationData":[OSD([subQ1,subQ0]),TDD([makeQuery(id+"F0.imprint","INTERSECT",VERTEX,{"disambiguationData":[OD(1.0)],"derivedFrom":[subQ1,subQ0]})])]});}
            var Q23;
            {var subQ0=sQuery(id+"F0.wireOp",EDGE,"E15.2.5.0");var subQ1=sQuery(id+"F0.wireOp",EDGE,"E8.0");Q23=makeQuery(id+"F2.opExtrude","SWEPT_EDGE",EDGE,{"disambiguationData":[OSD([subQ1,subQ0]),TDD([makeQuery(id+"F0.imprint","INTERSECT",VERTEX,{"disambiguationData":[OD(1.0)],"derivedFrom":[subQ1,subQ0]})])]});}
            fillet(context, id + "F9", {"entities" : qUnion([Q0, Q1, Q2, Q3, Q4, Q5, Q6, Q7, Q8, Q9, Q10, Q11, Q12, Q13, Q14, Q15, Q16, Q17, Q18, Q19, Q20, Q21, Q22, Q23]), "radius" : 2 * mm, "tangentPropagation" : true, "allowEdgeOverflow" : false});
        }
        {
            var Q0;
            Q0=makeQuery(id+"F6.opExtrude","CAP_EDGE",EDGE,{"disambiguationData":[OSD([sQuery(id+"F5.wireOp",EDGE,"E28")])],"isStart":false});
            var Q1;
            Q1=makeQuery(id+"F6.opExtrude","CAP_EDGE",EDGE,{"disambiguationData":[OSD([sQuery(id+"F5.wireOp",EDGE,"E28")])],"isStart":true});
            fillet(context, id + "F10", {"entities" : qUnion([Q0, Q1]), "radius" : 1 * mm, "tangentPropagation" : true, "allowEdgeOverflow" : false});
        }
        {
            var Q0;
            Q0=makeQuery(id+"F1.opExtrude","SWEPT_EDGE",EDGE,{"disambiguationData":[OSD([sQuery(id+"F0.wireOp",EDGE,"E3"),sQuery(id+"F0.wireOp",EDGE,"E13")])]});
            var Q1;
            Q1=makeQuery(id+"F1.opExtrude","SWEPT_EDGE",EDGE,{"disambiguationData":[OSD([sQuery(id+"F0.wireOp",EDGE,"E3"),sQuery(id+"F0.wireOp",EDGE,"E12")])]});
            fillet(context, id + "F11", {"entities" : qUnion([Q0, Q1]), "radius" : 5 * mm, "tangentPropagation" : true, "allowEdgeOverflow" : false});
        }
    });
